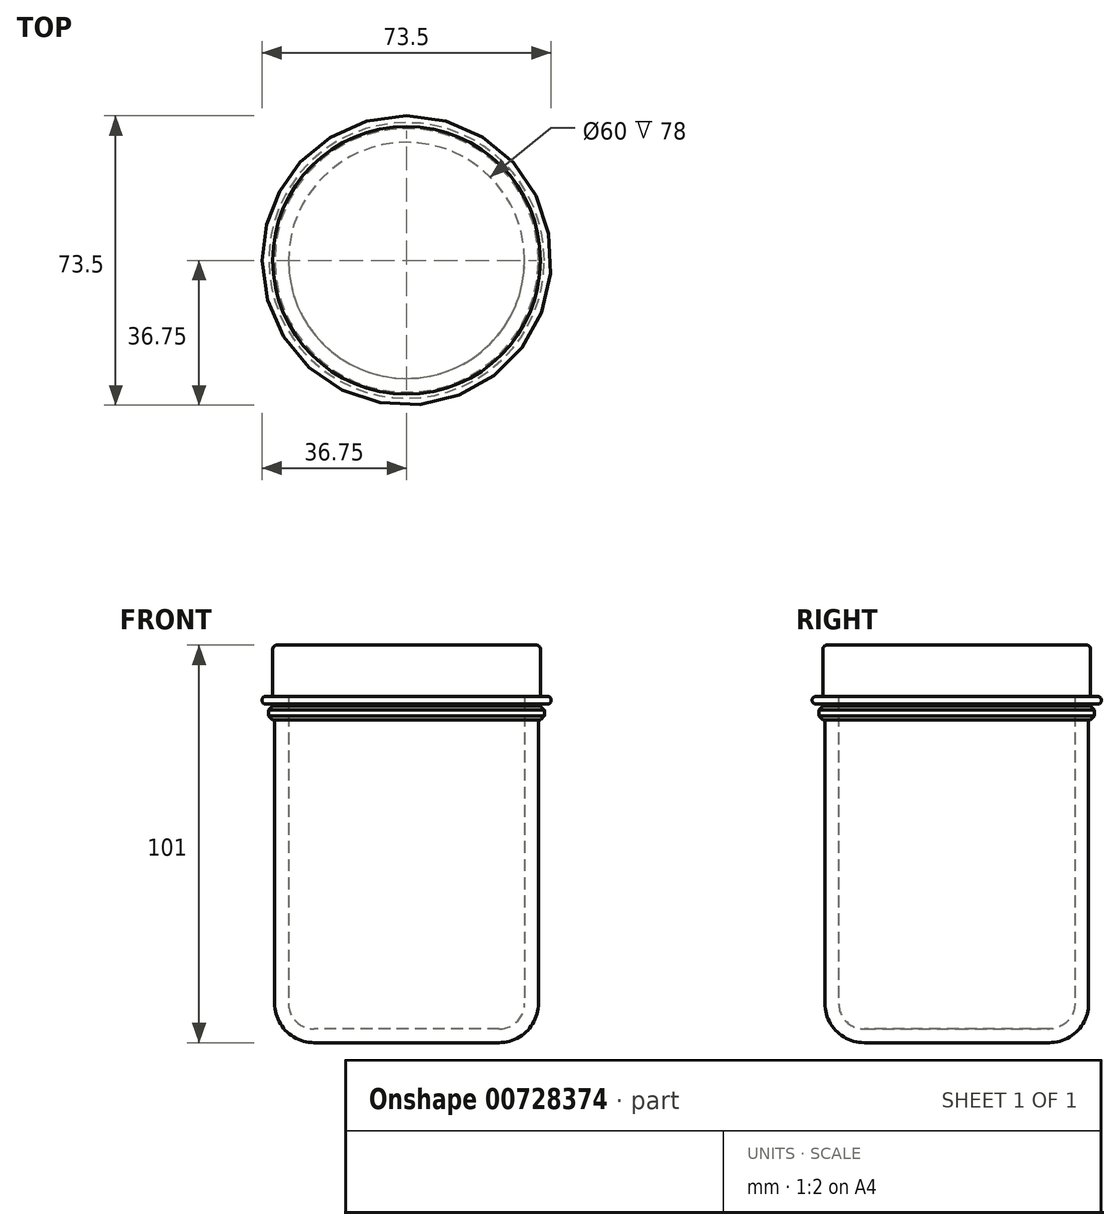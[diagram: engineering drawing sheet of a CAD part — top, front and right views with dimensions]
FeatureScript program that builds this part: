
annotation { "Feature Type Name" : "Feature", "Feature Type Description" : "" }
export const myFeature = defineFeature(function(context is Context, id is Id, definition is map)
    precondition{}
    {
        {
            var Q0;
            Q0=qCreatedBy(makeId("Top.planeOp"),FACE);
            var sketch = newSketch(context, id + "F0", { "sketchPlane" : qUnion([Q0])});
            skCircle(sketch, "E0", {"center": v(0, 0) * mm, "radius": 33.5 * mm});
            skSolve(sketch);
        }
        {
            var Q0;
            Q0=makeQuery(id+"F0.imprint","IMPRINT",FACE,{"disambiguationData":[TD([[makeQuery(id+"F0.imprint","IMPRINT",EDGE,{"derivedFrom":sQuery(id+"F0.wireOp",EDGE,"E0")}),1.0]])]});
            extrude(context, id + "F1", {"entities" : qUnion([Q0]), "depth" : 82 * mm, "offsetDistance" : 25 * mm});
        }
        {
            var Q0;
            Q0=makeQuery(id+"F1.opExtrude","CAP_EDGE",EDGE,{"disambiguationData":[OSD([sQuery(id+"F0.wireOp",EDGE,"E0")])],"isStart":true});
            fillet(context, id + "F2", {"entities" : qUnion([Q0]), "radius" : 10 * mm, "tangentPropagation" : true, "allowEdgeOverflow" : false});
        }
        {
            var Q0;
            Q0=makeQuery(id+"F1.opExtrude","CAP_FACE",FACE,{"disambiguationData":[OSD([sQuery(id+"F0.wireOp",EDGE,"E0")])],"isStart":false});
            var sketch = newSketch(context, id + "F3", { "sketchPlane" : qUnion([Q0])});
            skCircle(sketch, "E1", {"center": v(0, 0) * mm, "radius": 35 * mm});
            skSolve(sketch);
        }
        {
            var Q0;
            Q0=makeQuery(id+"F3.imprint","IMPRINT",FACE,{"disambiguationData":[TD([[makeQuery(id+"F3.imprint","IMPRINT",EDGE,{"derivedFrom":makeQuery(id+"F1.opExtrude","CAP_EDGE",EDGE,{"disambiguationData":[OSD([sQuery(id+"F0.wireOp",EDGE,"E0")])],"isStart":false})}),1.0]])]});
            extrude(context, id + "F4", {"entities" : qUnion([Q0]), "operationType" : NewBodyOperationType.ADD, "depth" : 18 * mm, "offsetDistance" : 25 * mm});
        }
        {
            var Q0;
            Q0=makeQuery(id+"F3.imprint","IMPRINT",FACE,{"disambiguationData":[TD([[makeQuery(id+"F3.imprint","IMPRINT",EDGE,{"derivedFrom":sQuery(id+"F3.wireOp",EDGE,"E1")}),1.0]])]});
            extrude(context, id + "F5", {"entities" : qUnion([Q0]), "operationType" : NewBodyOperationType.ADD, "depth" : 3.5 * mm, "offsetDistance" : 25 * mm});
        }
        {
            var Q0;
            Q0=makeQuery(id+"F5.opExtrude","CAP_EDGE",EDGE,{"disambiguationData":[OSD([sQuery(id+"F3.wireOp",EDGE,"E1")])],"isStart":false});
            var Q1;
            Q1=makeQuery(id+"F5.opExtrude","CAP_EDGE",EDGE,{"disambiguationData":[OSD([sQuery(id+"F3.wireOp",EDGE,"E1")])],"isStart":true});
            chamfer(context, id + "F6", {"entities" : qUnion([Q0, Q1]), "width" : 1 * mm, "tangentPropagation" : true});
        }
        {
            var Q0;
            Q0=makeQuery(id+"F4.opExtrude","CAP_FACE",FACE,{"disambiguationData":[OSD([sQuery(id+"F0.wireOp",EDGE,"E0")])],"isStart":false});
            shell(context, id + "F7", {"entities" : qUnion([Q0]), "thickness" : 3.5 * mm});
        }
        {
            var Q0;
            Q0=makeQuery(id+"F4.opExtrude","CAP_FACE",FACE,{"disambiguationData":[OSD([sQuery(id+"F0.wireOp",EDGE,"E0")])],"isStart":false});
            var sketch = newSketch(context, id + "F8", { "sketchPlane" : qUnion([Q0])});
            skCircle(sketch, "E2", {"center": v(0, 0) * mm, "radius": 34 * mm});
            skSolve(sketch);
        }
        {
            var Q0;
            {var subQ0=sQuery(id+"F0.wireOp",EDGE,"E0");Q0=makeQuery(id+"F8.imprint","IMPRINT",FACE,{"disambiguationData":[TD([[makeQuery(id+"F8.imprint","IMPRINT",EDGE,{"derivedFrom":makeQuery(id+"F7.opShell","OFFSET_EDGE",EDGE,{"disambiguationData":[OSD([subQ0]),TDD([makeQuery(id+"F4.opExtrude","CAP_EDGE",EDGE,{"disambiguationData":[OSD([subQ0])],"isStart":false})])]})}),1.0]])]});}
            var Q1;
            {var subQ0=sQuery(id+"F0.wireOp",EDGE,"E0");var subQ1=makeQuery(id+"F4.opExtrude","CAP_EDGE",EDGE,{"disambiguationData":[OSD([subQ0])],"isStart":false});Q1=makeQuery(id+"F8.imprint","IMPRINT",FACE,{"disambiguationData":[TD([[makeQuery(id+"F8.imprint","IMPRINT",EDGE,{"derivedFrom":subQ1}),1.0]])]});}
            var Q2;
            Q2=makeQuery(id+"F8.imprint","IMPRINT",FACE,{"disambiguationData":[TD([[makeQuery(id+"F8.imprint","IMPRINT",EDGE,{"derivedFrom":sQuery(id+"F8.wireOp",EDGE,"E2")}),1.0]])]});
            extrude(context, id + "F9", {"entities" : qUnion([Q0, Q1, Q2]), "depth" : 1 * mm, "offsetDistance" : 25 * mm});
        }
        {
            var Q0;
            Q0=makeQuery(id+"F9.opExtrude","CAP_FACE",FACE,{"disambiguationData":[OSD([sQuery(id+"F8.wireOp",EDGE,"E2")])],"isStart":true});
            extrude(context, id + "F10", {"entities" : qUnion([Q0]), "operationType" : NewBodyOperationType.ADD, "depth" : 12 * mm, "offsetDistance" : 25 * mm});
        }
        {
            var Q0;
            Q0=makeQuery(id+"F10.opExtrude","CAP_FACE",FACE,{"disambiguationData":[OSD([sQuery(id+"F8.wireOp",EDGE,"E2")])],"isStart":false});
            var sketch = newSketch(context, id + "F11", { "sketchPlane" : qUnion([Q0])});
            skCircle(sketch, "E3", {"center": v(0, 0) * mm, "radius": 36.75 * mm});
            skSolve(sketch);
        }
        {
            var Q0;
            Q0=makeQuery(id+"F11.imprint","IMPRINT",FACE,{"disambiguationData":[TD([[makeQuery(id+"F11.imprint","IMPRINT",EDGE,{"derivedFrom":sQuery(id+"F11.wireOp",EDGE,"E3")}),1.0]])]});
            var Q1;
            Q1=makeQuery(id+"F11.imprint","IMPRINT",FACE,{"disambiguationData":[TD([[makeQuery(id+"F11.imprint","IMPRINT",EDGE,{"derivedFrom":makeQuery(id+"F10.opExtrude","CAP_EDGE",EDGE,{"disambiguationData":[OSD([sQuery(id+"F8.wireOp",EDGE,"E2")])],"isStart":false})}),-1.0]])]});
            extrude(context, id + "F12", {"entities" : qUnion([Q0, Q1]), "operationType" : NewBodyOperationType.ADD, "depth" : 2 * mm, "offsetDistance" : 25 * mm});
        }
        {
            var Q0;
            Q0=makeQuery(id+"F12.opExtrude","CAP_EDGE",EDGE,{"disambiguationData":[OSD([sQuery(id+"F11.wireOp",EDGE,"E3")])],"isStart":true});
            fillet(context, id + "F13", {"entities" : qUnion([Q0]), "radius" : 1 * mm, "tangentPropagation" : true, "allowEdgeOverflow" : false});
        }
        {
            var Q0;
            Q0=makeQuery(id+"F12.opExtrude","CAP_EDGE",EDGE,{"disambiguationData":[OSD([sQuery(id+"F11.wireOp",EDGE,"E3")])],"isStart":false});
            fillet(context, id + "F14", {"entities" : qUnion([Q0]), "radius" : 1 * mm, "tangentPropagation" : true, "allowEdgeOverflow" : false});
        }
        {
            var Q0;
            Q0=makeQuery(id+"F10.opExtrude","CAP_EDGE",EDGE,{"disambiguationData":[OSD([sQuery(id+"F8.wireOp",EDGE,"E2")])],"isStart":false});
            var Q1;
            Q1=makeQuery(id+"F9.opExtrude","CAP_EDGE",EDGE,{"disambiguationData":[OSD([sQuery(id+"F8.wireOp",EDGE,"E2")])],"isStart":false});
            fillet(context, id + "F15", {"entities" : qUnion([Q0, Q1]), "radius" : 1 * mm, "tangentPropagation" : true, "allowEdgeOverflow" : false});
        }
    });
